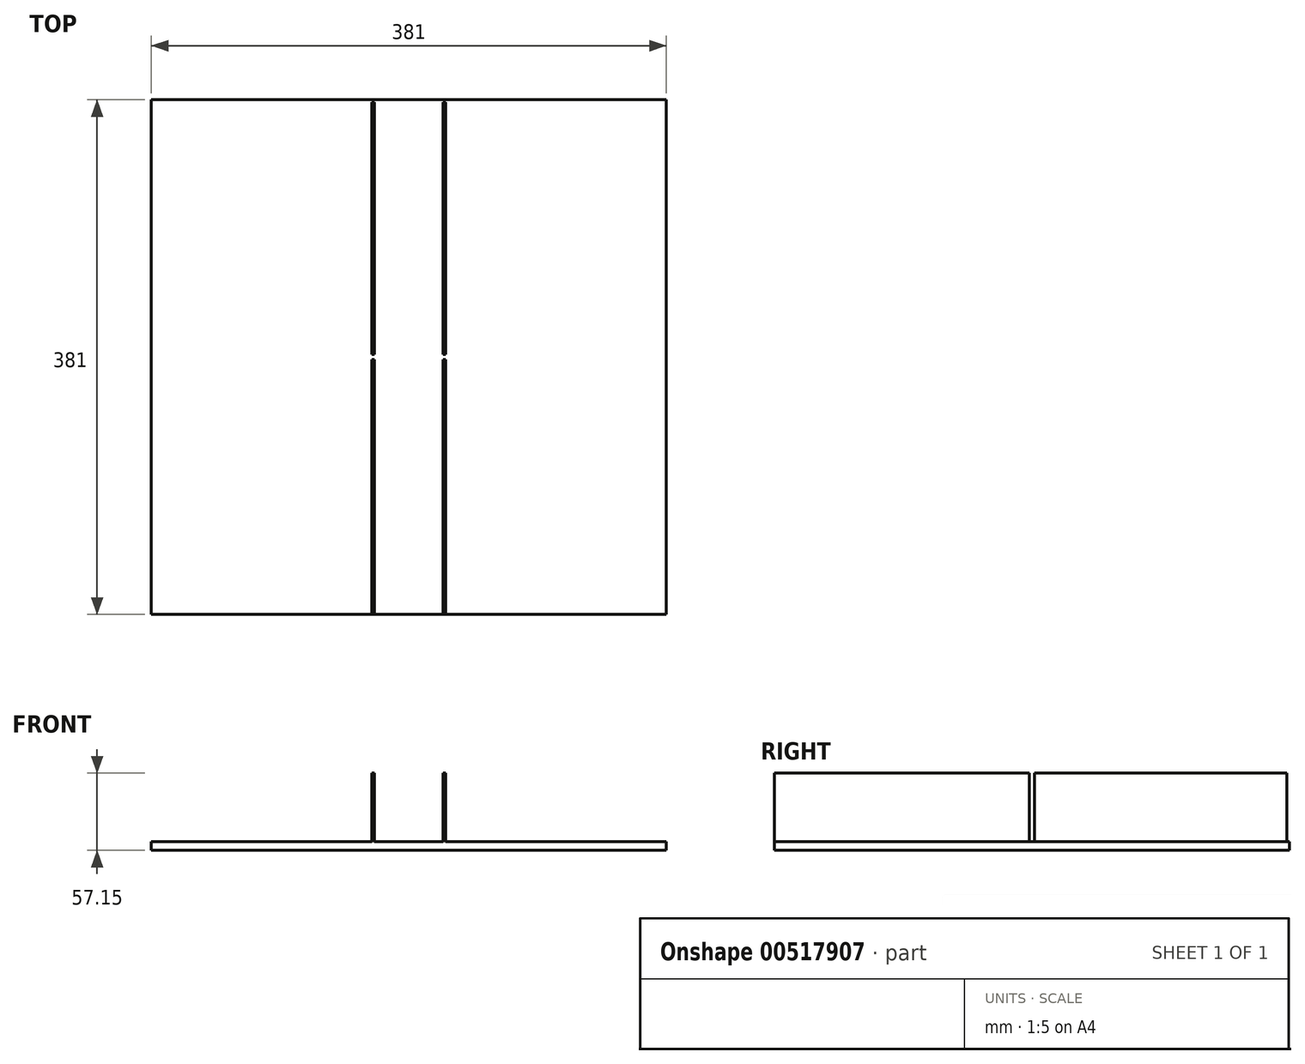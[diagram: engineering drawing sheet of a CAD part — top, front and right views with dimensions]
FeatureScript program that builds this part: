
annotation { "Feature Type Name" : "Feature", "Feature Type Description" : "" }
export const myFeature = defineFeature(function(context is Context, id is Id, definition is map)
    precondition{}
    {
        {
            var Q0;
            Q0=qCreatedBy(makeId("Top.planeOp"),FACE);
            var sketch = newSketch(context, id + "F0", { "sketchPlane" : qUnion([Q0])});
            skLineSegment(sketch, "E0.bottom", {"start": v(-185.97, 216.23) * mm, "end": v(195.03, 216.23) * mm});
            skLineSegment(sketch, "E0.top", {"start": v(-185.97, -164.77) * mm, "end": v(195.03, -164.77) * mm});
            skLineSegment(sketch, "E0.left", {"start": v(-185.97, 216.23) * mm, "end": v(-185.97, -164.77) * mm});
            skLineSegment(sketch, "E0.right", {"start": v(195.03, 216.23) * mm, "end": v(195.03, -164.77) * mm});
            skSolve(sketch);
        }
        {
            var Q0;
            Q0=makeQuery(id+"F0.imprint","IMPRINT",FACE,{"disambiguationData":[TD([[makeQuery(id+"F0.imprint","IMPRINT",EDGE,{"derivedFrom":sQuery(id+"F0.wireOp",EDGE,"E0.bottom")}),-1.0]])]});
            extrude(context, id + "F1", {"entities" : qUnion([Q0]), "depth" : 6.35 * mm, "offsetDistance" : 25.4 * mm});
        }
        {
            var Q0;
            Q0=makeQuery(id+"F1.opExtrude","CAP_FACE",FACE,{"disambiguationData":[OSD([sQuery(id+"F0.wireOp",EDGE,"E0.bottom"),sQuery(id+"F0.wireOp",EDGE,"E0.top"),sQuery(id+"F0.wireOp",EDGE,"E0.left"),sQuery(id+"F0.wireOp",EDGE,"E0.right")])],"isStart":false});
            var sketch = newSketch(context, id + "F2", { "sketchPlane" : qUnion([Q0])});
            skLineSegment(sketch, "E1", {"start": v(-185.97, 25.73) * mm, "end": v(-20.87, 25.73) * mm});
            skLineSegment(sketch, "E2.0", {"start": v(-20.87, 216.23) * mm, "end": v(-20.87, -164.77) * mm});
            skLineSegment(sketch, "E3.MirrorCS", {"start": v(29.93, 216.23) * mm, "end": v(29.93, -164.77) * mm});
            skPoint(sketch, "E4.orphan", {"position": v(4.53, 216.23) * mm});
            skLineSegment(sketch, "E5.trimOffspring", {"start": v(29.93, 25.73) * mm, "end": v(195.03, 25.73) * mm});
            skPoint(sketch, "E6.end.orphan", {"position": v(4.53, -164.77) * mm});
            skLineSegment(sketch, "E7.0", {"start": v(-184.06, 214.33) * mm, "end": v(193.13, 214.33) * mm});
            skLineSegment(sketch, "E7.1", {"start": v(-184.06, 214.33) * mm, "end": v(-184.06, -162.86) * mm});
            skLineSegment(sketch, "E7.2", {"start": v(-184.06, -162.86) * mm, "end": v(193.13, -162.86) * mm});
            skLineSegment(sketch, "E7.3", {"start": v(193.13, 214.33) * mm, "end": v(193.13, -162.86) * mm});
            skLineSegment(sketch, "E8.0", {"start": v(-185.97, 23.83) * mm, "end": v(-20.87, 23.83) * mm});
            skLineSegment(sketch, "E9.MirrorCS", {"start": v(-185.97, 27.64) * mm, "end": v(-20.87, 27.64) * mm});
            skLineSegment(sketch, "E10.0", {"start": v(29.93, 23.83) * mm, "end": v(195.03, 23.83) * mm});
            skLineSegment(sketch, "E11.MirrorCS", {"start": v(29.93, 27.64) * mm, "end": v(195.03, 27.64) * mm});
            skLineSegment(sketch, "E12.0", {"start": v(-22.77, 216.23) * mm, "end": v(-22.77, -164.77) * mm});
            skLineSegment(sketch, "E13.0", {"start": v(31.84, 216.23) * mm, "end": v(31.84, -164.77) * mm});
            skSolve(sketch);
        }
        {
            var Q0;
            {var subQ0=sQuery(id+"F2.wireOp",EDGE,"E8.0");var subQ1=sQuery(id+"F2.wireOp",EDGE,"E2.0");var subQ2=makeQuery(id+"F2.imprint","INTERSECT",VERTEX,{"derivedFrom":[subQ1,subQ0]});Q0=makeQuery(id+"F2.imprint","IMPRINT",FACE,{"disambiguationData":[TD([[makeQuery(id+"F2.imprint","IMPRINT",EDGE,{"disambiguationData":[TD([[subQ2,-1.0]])],"derivedFrom":subQ1}),-1.0]])]});}
            var Q1;
            {var subQ0=sQuery(id+"F2.wireOp",EDGE,"E10.0");var subQ1=sQuery(id+"F2.wireOp",EDGE,"E3.MirrorCS");var subQ2=makeQuery(id+"F2.imprint","INTERSECT",VERTEX,{"derivedFrom":[subQ1,subQ0]});Q1=makeQuery(id+"F2.imprint","IMPRINT",FACE,{"disambiguationData":[TD([[makeQuery(id+"F2.imprint","IMPRINT",EDGE,{"disambiguationData":[TD([[subQ2,-1.0]])],"derivedFrom":subQ1}),1.0]])]});}
            var Q2;
            {var subQ0=sQuery(id+"F2.wireOp",EDGE,"E3.MirrorCS");var subQ1=makeQuery(id+"F1.opExtrude","CAP_EDGE",EDGE,{"disambiguationData":[OSD([sQuery(id+"F0.wireOp",EDGE,"E0.top")])],"isStart":false});var subQ2=makeQuery(id+"F2.imprint","INTERSECT",VERTEX,{"derivedFrom":[subQ1,subQ0]});Q2=makeQuery(id+"F2.imprint","IMPRINT",FACE,{"disambiguationData":[TD([[makeQuery(id+"F2.imprint","IMPRINT",EDGE,{"disambiguationData":[TD([[subQ2,1.0]])],"derivedFrom":subQ0}),1.0]])]});}
            var Q3;
            {var subQ0=sQuery(id+"F2.wireOp",EDGE,"E2.0");var subQ1=makeQuery(id+"F1.opExtrude","CAP_EDGE",EDGE,{"disambiguationData":[OSD([sQuery(id+"F0.wireOp",EDGE,"E0.top")])],"isStart":false});var subQ2=makeQuery(id+"F2.imprint","INTERSECT",VERTEX,{"derivedFrom":[subQ1,subQ0]});Q3=makeQuery(id+"F2.imprint","IMPRINT",FACE,{"disambiguationData":[TD([[makeQuery(id+"F2.imprint","IMPRINT",EDGE,{"disambiguationData":[TD([[subQ2,1.0]])],"derivedFrom":subQ0}),-1.0]])]});}
            var Q4;
            {var subQ0=sQuery(id+"F2.wireOp",EDGE,"E11.MirrorCS");var subQ1=sQuery(id+"F2.wireOp",EDGE,"E3.MirrorCS");var subQ2=makeQuery(id+"F2.imprint","INTERSECT",VERTEX,{"derivedFrom":[subQ1,subQ0]});Q4=makeQuery(id+"F2.imprint","IMPRINT",FACE,{"disambiguationData":[TD([[makeQuery(id+"F2.imprint","IMPRINT",EDGE,{"disambiguationData":[TD([[subQ2,1.0]])],"derivedFrom":subQ1}),1.0]])]});}
            var Q5;
            {var subQ0=sQuery(id+"F2.wireOp",EDGE,"E9.MirrorCS");var subQ1=sQuery(id+"F2.wireOp",EDGE,"E2.0");var subQ2=makeQuery(id+"F2.imprint","INTERSECT",VERTEX,{"derivedFrom":[subQ1,subQ0]});Q5=makeQuery(id+"F2.imprint","IMPRINT",FACE,{"disambiguationData":[TD([[makeQuery(id+"F2.imprint","IMPRINT",EDGE,{"disambiguationData":[TD([[subQ2,1.0]])],"derivedFrom":subQ1}),-1.0]])]});}
            extrude(context, id + "F3", {"entities" : qUnion([Q0, Q1, Q2, Q3, Q4, Q5]), "operationType" : NewBodyOperationType.ADD, "depth" : 50.8 * mm, "offsetDistance" : 25.4 * mm});
        }
    });
